# Revit family: CC 150
name_source: partatom
category: Mechanical Equipment
units: mm (PartAtom-declared; Revit-internal decimal feet)

## family parameters
Always vertical = Yes
Cut with Voids When Loaded = No
OmniClass Number = 23.75.00.00
OmniClass Title = Climate Control (HVAC)
Part Type = Normal
Room Calculation Point = No
Round Connector Dimension = Use Diameter
Shared = No
Work Plane-Based = No

## types (1)
- CC 150
    Condensate = 12 mm  [stored 0.0393701 ft]
    Electrical connection = 1 ~ 230 V / N / PE / 50 Hz
    Exhaust Air = 125 mm
    L-C Duct Exhaust = 105 mm  [stored 0.344488 ft]
    Manufacturer = Airmaster A/S
    Max. flow rate 30 dB(A) with ePM10 50% filters = 115 m³
    Max. flow rate 30 dB(A) with ePM10 55% filters = 90 m³
    Max. flow rate 30 dB(A) with ePM10 80% filters = 85 m³
    Max. flow rate 35 dB(A) with ePM10 50% filters = 147 m³
    Max. flow rate 35 dB(A) with ePM10 55% filters = 126 m³
    Max. flow rate 35 dB(A) with ePM10 80% filters = 115 m³
    Model = CC 150
    Nominal current,Cooling = 2,17 A
    Phase 1 - Max Current = 2,17 A
    Phase 1 - Max Power Consumption = 500 W
    R-C Duct Supply = 105 mm  [stored 0.344488 ft]
    Suply Air In = 125 mm
    T-C Duct Exhaust = 158 mm
    T-C Duct Supply = 158 mm
    Total Depth = 859 mm  [stored 2.81824 ft]
    Total Hight = 262 mm  [stored 0.85958 ft]
    Total Width = 1170 mm  [stored 3.83858 ft]
    URL = www.airmaster-as.com
    Weight (Standard Unit) = 108

note: [stored X ft] marks values corroborated as IEEE doubles in the binary element streams (Revit-internal decimal feet)

## geometry (parser evidence)
native form markers: Sweep x5
no freeform markers — native parametric forms only
